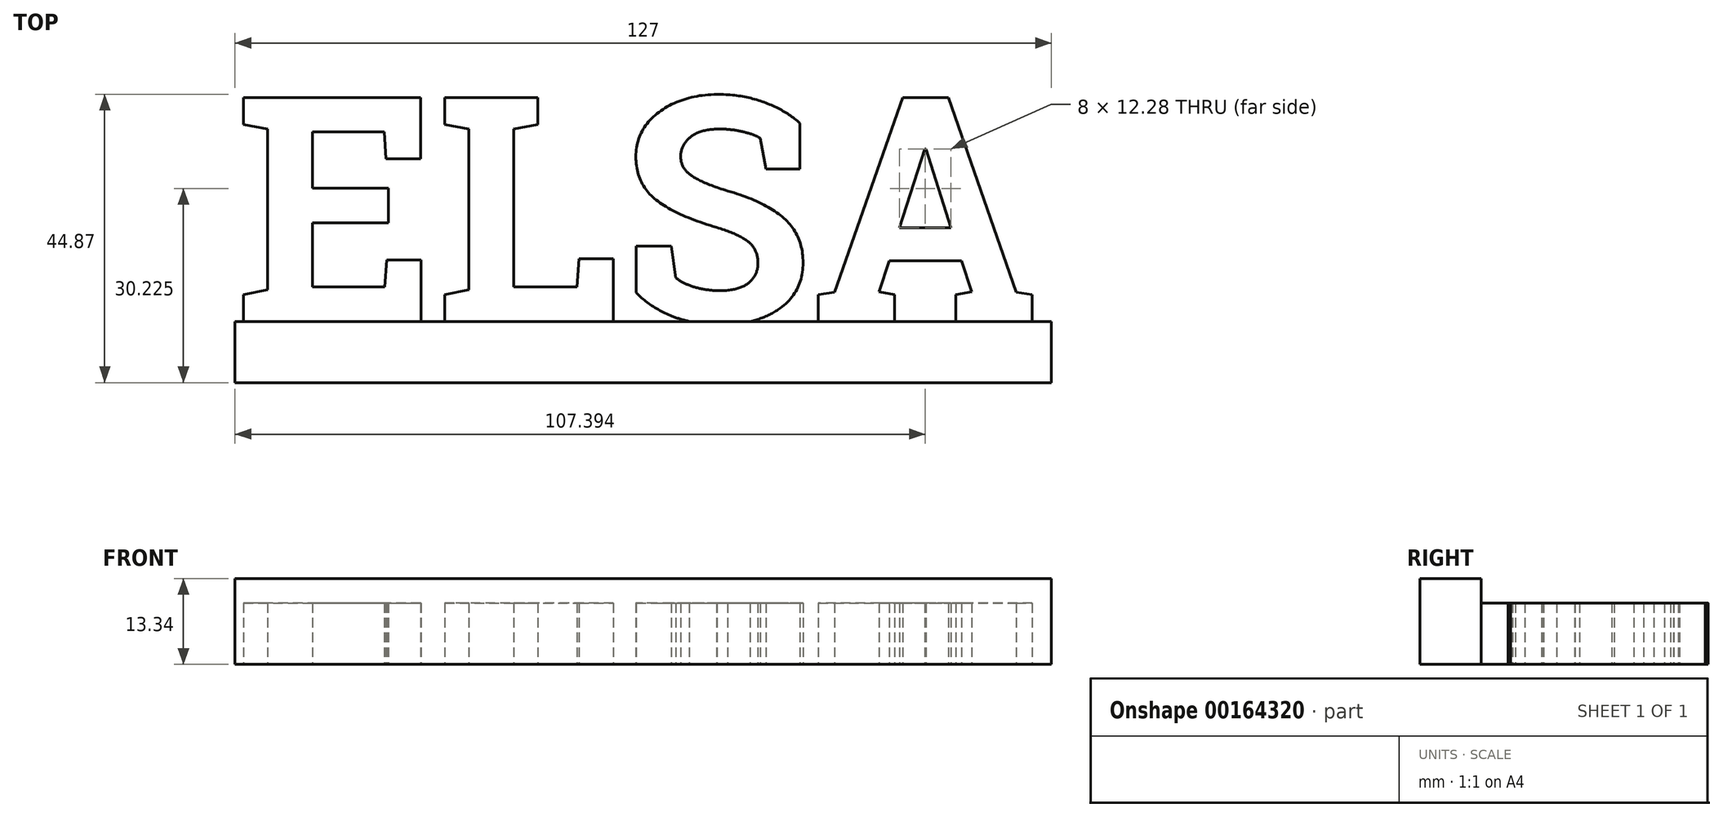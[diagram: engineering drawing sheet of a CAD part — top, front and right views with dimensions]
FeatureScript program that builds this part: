
annotation { "Feature Type Name" : "Feature", "Feature Type Description" : "" }
export const myFeature = defineFeature(function(context is Context, id is Id, definition is map)
    precondition{}
    {
        {
            var Q0;
            Q0=qCreatedBy(makeId("Top.planeOp"),FACE);
            var sketch = newSketch(context, id + "F0", { "sketchPlane" : qUnion([Q0])});
            skLineSegment(sketch, "E0.bottom", {"start": v(0, 0) * mm, "end": v(127, 0) * mm});
            skLineSegment(sketch, "E0.top", {"start": v(0, 9.53) * mm, "end": v(127, 9.53) * mm});
            skLineSegment(sketch, "E0.left", {"start": v(0, 0) * mm, "end": v(0, 9.53) * mm});
            skLineSegment(sketch, "E0.right", {"start": v(127, 0) * mm, "end": v(127, 9.53) * mm});
            skText(sketch, "E1", { "text": "ELSA", "fontName": "RobotoSlab-Bold.ttf"});
            const initialGuessF0  = {"E1": [0, 0.00953, 1, 0, 0.0353]};
            skSetInitialGuess(sketch, initialGuessF0);
            skSolve(sketch);
        }
        {
            var Q0;
            Q0=qSketchRegion(id+"F0",true);
            extrude(context, id + "F1", {"entities" : qUnion([Q0]), "depth" : 9.52 * mm});
        }
        {
            var Q0;
            Q0=makeQuery(id+"F1.opExtrude","CAP_FACE",FACE,{"disambiguationData":[OSD([sQuery(id+"F0.wireOp",EDGE,"E0.bottom"),sQuery(id+"F0.wireOp",EDGE,"E0.top"),sQuery(id+"F0.wireOp",EDGE,"E0.left"),sQuery(id+"F0.wireOp",EDGE,"E0.right"),sQuery(id+"F0.wireOp",EDGE,"E1.sketch_text.stroke-0"),sQuery(id+"F0.wireOp",EDGE,"E1.sketch_text.stroke-1"),sQuery(id+"F0.wireOp",EDGE,"E1.sketch_text.stroke-2"),sQuery(id+"F0.wireOp",EDGE,"E1.sketch_text.stroke-3"),sQuery(id+"F0.wireOp",EDGE,"E1.sketch_text.stroke-4"),sQuery(id+"F0.wireOp",EDGE,"E1.sketch_text.stroke-5"),sQuery(id+"F0.wireOp",EDGE,"E1.sketch_text.stroke-6"),sQuery(id+"F0.wireOp",EDGE,"E1.sketch_text.stroke-7"),sQuery(id+"F0.wireOp",EDGE,"E1.sketch_text.stroke-8"),sQuery(id+"F0.wireOp",EDGE,"E1.sketch_text.stroke-9"),sQuery(id+"F0.wireOp",EDGE,"E1.sketch_text.stroke-10"),sQuery(id+"F0.wireOp",EDGE,"E1.sketch_text.stroke-11"),sQuery(id+"F0.wireOp",EDGE,"E1.sketch_text.stroke-12"),sQuery(id+"F0.wireOp",EDGE,"E1.sketch_text.stroke-13"),sQuery(id+"F0.wireOp",EDGE,"E1.sketch_text.stroke-14"),sQuery(id+"F0.wireOp",EDGE,"E1.sketch_text.stroke-15"),sQuery(id+"F0.wireOp",EDGE,"E1.sketch_text.stroke-16"),sQuery(id+"F0.wireOp",EDGE,"E1.sketch_text.stroke-17"),sQuery(id+"F0.wireOp",EDGE,"E1.sketch_text.stroke-18"),sQuery(id+"F0.wireOp",EDGE,"E1.sketch_text.stroke-19"),sQuery(id+"F0.wireOp",EDGE,"E1.sketch_text.stroke-20"),sQuery(id+"F0.wireOp",EDGE,"E1.sketch_text.stroke-21"),sQuery(id+"F0.wireOp",EDGE,"E1.sketch_text.stroke-22"),sQuery(id+"F0.wireOp",EDGE,"E1.sketch_text.stroke-23"),sQuery(id+"F0.wireOp",EDGE,"E1.sketch_text.stroke-24"),sQuery(id+"F0.wireOp",EDGE,"E1.sketch_text.stroke-25"),sQuery(id+"F0.wireOp",EDGE,"E1.sketch_text.stroke-26"),sQuery(id+"F0.wireOp",EDGE,"E1.sketch_text.stroke-27"),sQuery(id+"F0.wireOp",EDGE,"E1.sketch_text.stroke-28"),sQuery(id+"F0.wireOp",EDGE,"E1.sketch_text.stroke-29"),sQuery(id+"F0.wireOp",EDGE,"E1.sketch_text.stroke-30"),sQuery(id+"F0.wireOp",EDGE,"E1.sketch_text.stroke-31"),sQuery(id+"F0.wireOp",EDGE,"E1.sketch_text.stroke-32"),sQuery(id+"F0.wireOp",EDGE,"E1.sketch_text.stroke-33"),sQuery(id+"F0.wireOp",EDGE,"E1.sketch_text.stroke-34"),sQuery(id+"F0.wireOp",EDGE,"E1.sketch_text.stroke-35"),sQuery(id+"F0.wireOp",EDGE,"E1.sketch_text.stroke-36"),sQuery(id+"F0.wireOp",EDGE,"E1.sketch_text.stroke-37"),sQuery(id+"F0.wireOp",EDGE,"E1.sketch_text.stroke-38"),sQuery(id+"F0.wireOp",EDGE,"E1.sketch_text.stroke-39"),sQuery(id+"F0.wireOp",EDGE,"E1.sketch_text.stroke-40"),sQuery(id+"F0.wireOp",EDGE,"E1.sketch_text.stroke-42"),sQuery(id+"F0.wireOp",EDGE,"E1.sketch_text.stroke-43"),sQuery(id+"F0.wireOp",EDGE,"E1.sketch_text.stroke-44"),sQuery(id+"F0.wireOp",EDGE,"E1.sketch_text.stroke-45"),sQuery(id+"F0.wireOp",EDGE,"E1.sketch_text.stroke-46"),sQuery(id+"F0.wireOp",EDGE,"E1.sketch_text.stroke-47"),sQuery(id+"F0.wireOp",EDGE,"E1.sketch_text.stroke-48"),sQuery(id+"F0.wireOp",EDGE,"E1.sketch_text.stroke-50"),sQuery(id+"F0.wireOp",EDGE,"E1.sketch_text.stroke-51"),sQuery(id+"F0.wireOp",EDGE,"E1.sketch_text.stroke-52"),sQuery(id+"F0.wireOp",EDGE,"E1.sketch_text.stroke-53"),sQuery(id+"F0.wireOp",EDGE,"E1.sketch_text.stroke-54"),sQuery(id+"F0.wireOp",EDGE,"E1.sketch_text.stroke-55"),sQuery(id+"F0.wireOp",EDGE,"E1.sketch_text.stroke-56"),sQuery(id+"F0.wireOp",EDGE,"E1.sketch_text.stroke-57"),sQuery(id+"F0.wireOp",EDGE,"E1.sketch_text.stroke-58"),sQuery(id+"F0.wireOp",EDGE,"E1.sketch_text.stroke-59"),sQuery(id+"F0.wireOp",EDGE,"E1.sketch_text.stroke-60"),sQuery(id+"F0.wireOp",EDGE,"E1.sketch_text.stroke-62"),sQuery(id+"F0.wireOp",EDGE,"E1.sketch_text.stroke-63"),sQuery(id+"F0.wireOp",EDGE,"E1.sketch_text.stroke-64"),sQuery(id+"F0.wireOp",EDGE,"E1.sketch_text.stroke-65"),sQuery(id+"F0.wireOp",EDGE,"E1.sketch_text.stroke-66"),sQuery(id+"F0.wireOp",EDGE,"E1.sketch_text.stroke-67"),sQuery(id+"F0.wireOp",EDGE,"E1.sketch_text.stroke-68"),sQuery(id+"F0.wireOp",EDGE,"E1.sketch_text.stroke-69"),sQuery(id+"F0.wireOp",EDGE,"E1.sketch_text.stroke-70"),sQuery(id+"F0.wireOp",EDGE,"E1.sketch_text.stroke-71"),sQuery(id+"F0.wireOp",EDGE,"E1.sketch_text.stroke-72"),sQuery(id+"F0.wireOp",EDGE,"E1.sketch_text.stroke-73"),sQuery(id+"F0.wireOp",EDGE,"E1.sketch_text.stroke-75"),sQuery(id+"F0.wireOp",EDGE,"E1.sketch_text.stroke-76"),sQuery(id+"F0.wireOp",EDGE,"E1.sketch_text.stroke-77"),sQuery(id+"F0.wireOp",EDGE,"E1.sketch_text.stroke-78"),sQuery(id+"F0.wireOp",EDGE,"E1.sketch_text.stroke-79"),sQuery(id+"F0.wireOp",EDGE,"E1.sketch_text.stroke-80"),sQuery(id+"F0.wireOp",EDGE,"E1.sketch_text.stroke-81"),sQuery(id+"F0.wireOp",EDGE,"E1.sketch_text.stroke-82"),sQuery(id+"F0.wireOp",EDGE,"E1.sketch_text.stroke-83"),sQuery(id+"F0.wireOp",EDGE,"E1.sketch_text.stroke-84"),sQuery(id+"F0.wireOp",EDGE,"E1.sketch_text.stroke-85"),sQuery(id+"F0.wireOp",EDGE,"E1.sketch_text.stroke-86"),sQuery(id+"F0.wireOp",EDGE,"E1.sketch_text.stroke-87"),sQuery(id+"F0.wireOp",EDGE,"E1.sketch_text.stroke-88")])],"isStart":false});
            var sketch = newSketch(context, id + "F2", { "sketchPlane" : qUnion([Q0])});
            skLineSegment(sketch, "E2.bottom", {"start": v(0, 0) * mm, "end": v(127, 0) * mm});
            skLineSegment(sketch, "E2.top", {"start": v(0, 9.53) * mm, "end": v(127, 9.53) * mm});
            skLineSegment(sketch, "E2.left", {"start": v(0, 0) * mm, "end": v(0, 9.53) * mm});
            skLineSegment(sketch, "E2.right", {"start": v(127, 0) * mm, "end": v(127, 9.53) * mm});
            skSolve(sketch);
        }
        {
            var Q0;
            Q0=qSketchRegion(id+"F2",true);
            extrude(context, id + "F3", {"entities" : qUnion([Q0]), "operationType" : NewBodyOperationType.ADD, "depth" : 3.8 * mm});
        }
    });
